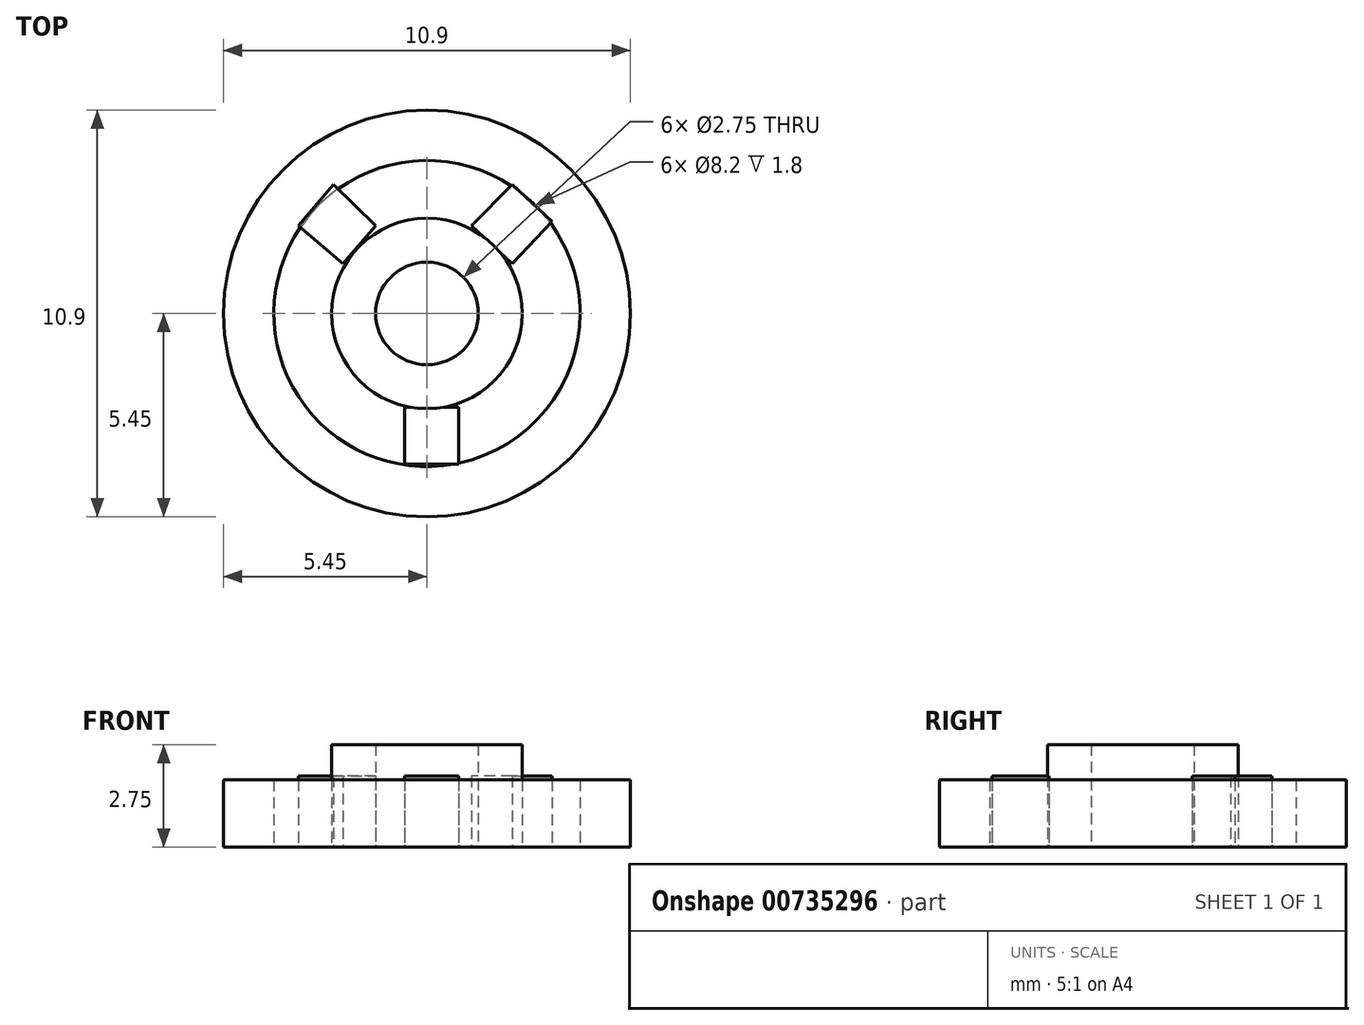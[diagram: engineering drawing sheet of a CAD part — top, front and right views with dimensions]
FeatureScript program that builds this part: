
annotation { "Feature Type Name" : "Feature", "Feature Type Description" : "" }
export const myFeature = defineFeature(function(context is Context, id is Id, definition is map)
    precondition{}
    {
        {
            var Q0;
            Q0=qCreatedBy(makeId("Top.planeOp"),FACE);
            var sketch = newSketch(context, id + "F0", { "sketchPlane" : qUnion([Q0])});
            skCircle(sketch, "E0", {"center": v(0, 0) * mm, "radius": 2.55 * mm});
            skCircle(sketch, "E1", {"center": v(0, 0) * mm, "radius": 1.37 * mm});
            skSolve(sketch);
        }
        {
            var Q0;
            Q0 = qSketchRegion(id + "F0", true);
            extrude(context, id + "F1", {"entities" : qUnion([Q0]), "depth" : 2.75 * mm, "offsetDistance" : 25 * mm});
        }
        {
            var Q0;
            Q0=qCreatedBy(makeId("Top.planeOp"),FACE);
            var sketch = newSketch(context, id + "F2", { "sketchPlane" : qUnion([Q0])});
            skCircle(sketch, "E2", {"center": v(0, 0) * mm, "radius": 5.45 * mm});
            skCircle(sketch, "E3", {"center": v(0, 0) * mm, "radius": 4.1 * mm});
            skSolve(sketch);
        }
        {
            var Q0;
            Q0 = qSketchRegion(id + "F2", true);
            extrude(context, id + "F3", {"entities" : qUnion([Q0]), "depth" : 1.8 * mm, "offsetDistance" : 25 * mm});
        }
        {
            var Q0;
            Q0=qCreatedBy(makeId("Top.planeOp"),FACE);
            var sketch = newSketch(context, id + "F4", { "sketchPlane" : qUnion([Q0])});
            skLineSegment(sketch, "E4.bottom", {"start": v(-0.6, -2.51) * mm, "end": v(0.85, -2.51) * mm});
            skLineSegment(sketch, "E4.top", {"start": v(-0.6, -4.03) * mm, "end": v(0.85, -4.03) * mm});
            skLineSegment(sketch, "E4.left", {"start": v(-0.6, -2.51) * mm, "end": v(-0.6, -4.03) * mm});
            skLineSegment(sketch, "E4.right", {"start": v(0.85, -2.51) * mm, "end": v(0.85, -4.03) * mm});
            skLineSegment(sketch, "E5", {"start": v(1.2, 2.35) * mm, "end": v(2.29, 1.33) * mm});
            skLineSegment(sketch, "E6", {"start": v(2.29, 1.33) * mm, "end": v(3.35, 2.47) * mm});
            skLineSegment(sketch, "E7", {"start": v(3.35, 2.47) * mm, "end": v(2.29, 3.45) * mm});
            skLineSegment(sketch, "E8", {"start": v(2.29, 3.45) * mm, "end": v(1.2, 2.35) * mm});
            skLineSegment(sketch, "E9", {"start": v(-1.37, 2.35) * mm, "end": v(-2.25, 1.33) * mm});
            skLineSegment(sketch, "E10", {"start": v(-2.25, 1.33) * mm, "end": v(-3.44, 2.35) * mm});
            skLineSegment(sketch, "E11", {"start": v(-3.44, 2.35) * mm, "end": v(-2.5, 3.45) * mm});
            skLineSegment(sketch, "E12", {"start": v(-2.5, 3.45) * mm, "end": v(-1.37, 2.35) * mm});
            skSolve(sketch);
        }
        {
            var Q0;
            Q0 = qSketchRegion(id + "F4", true);
            extrude(context, id + "F5", {"entities" : qUnion([Q0]), "depth" : 1.9 * mm, "offsetDistance" : 25 * mm});
        }
    });
